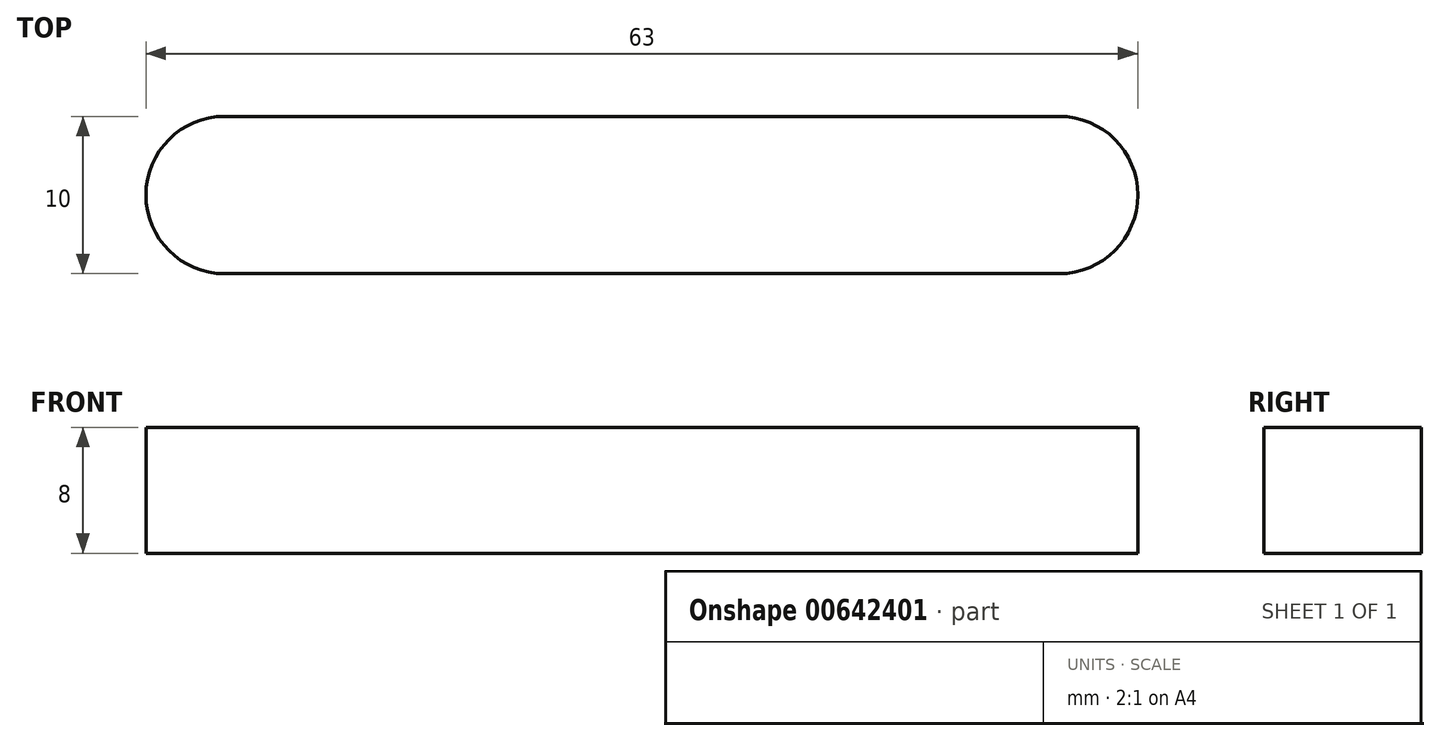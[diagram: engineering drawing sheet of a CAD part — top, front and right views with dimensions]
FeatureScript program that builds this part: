
annotation { "Feature Type Name" : "Feature", "Feature Type Description" : "" }
export const myFeature = defineFeature(function(context is Context, id is Id, definition is map)
    precondition{}
    {
        {
            var Q0;
            Q0=qCreatedBy(makeId("Top.planeOp"),FACE);
            var sketch = newSketch(context, id + "F0", { "sketchPlane" : qUnion([Q0])});
            skArc(sketch, "E0", {"start": v(0, 5) * mm, "mid": v(-5, 0) * mm, "end": v(0, -5) * mm});
            skArc(sketch, "E1", {"start": v(53, -5) * mm, "mid": v(58, 0) * mm, "end": v(53, 5) * mm});
            skLineSegment(sketch, "E2", {"start": v(0, 5) * mm, "end": v(53, 5) * mm});
            skLineSegment(sketch, "E3", {"start": v(0, -5) * mm, "end": v(53, -5) * mm});
            skSolve(sketch);
        }
        {
            var Q0;
            Q0=makeQuery(id+"F0.imprint","IMPRINT",FACE,{"disambiguationData":[TD([[makeQuery(id+"F0.imprint","IMPRINT",EDGE,{"derivedFrom":sQuery(id+"F0.wireOp",EDGE,"E0")}),1.0]])]});
            extrude(context, id + "F1", {"entities" : qUnion([Q0]), "depth" : 8 * mm, "offsetDistance" : 25 * mm});
        }
    });
